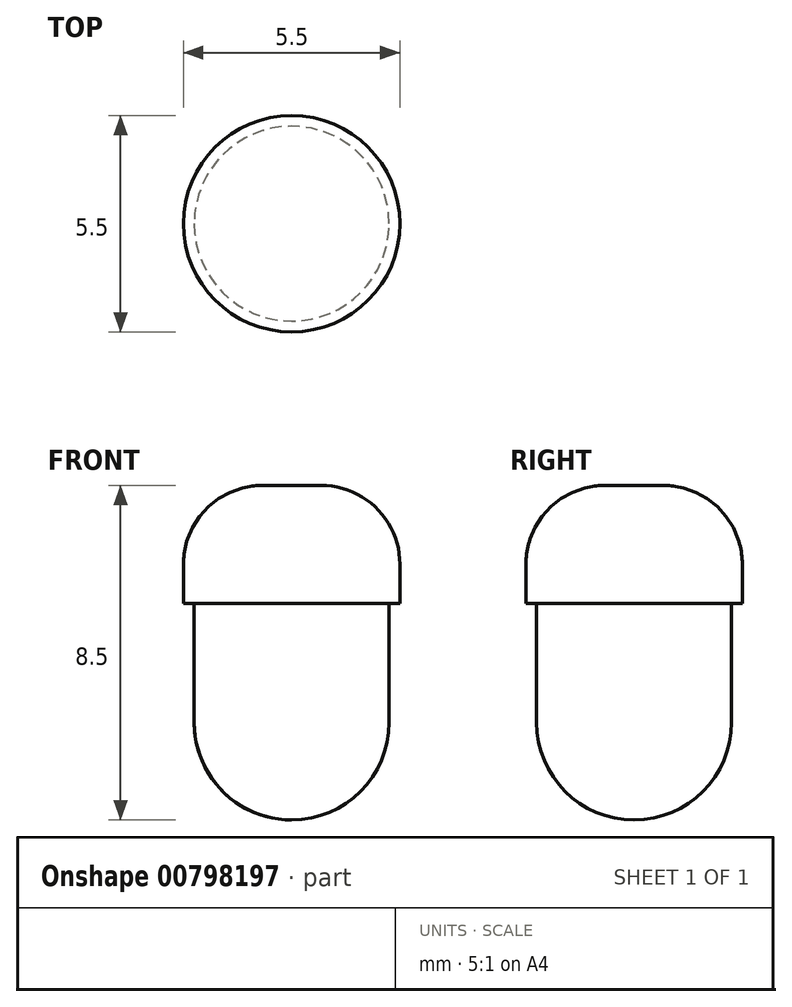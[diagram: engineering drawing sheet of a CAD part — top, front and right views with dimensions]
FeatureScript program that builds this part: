
annotation { "Feature Type Name" : "Feature", "Feature Type Description" : "" }
export const myFeature = defineFeature(function(context is Context, id is Id, definition is map)
    precondition{}
    {
        {
            var Q0;
            Q0=qCreatedBy(makeId("Top.planeOp"),FACE);
            var sketch = newSketch(context, id + "F0", { "sketchPlane" : qUnion([Q0])});
            skCircle(sketch, "E0", {"center": v(0, 0) * mm, "radius": 2.75 * mm});
            skSolve(sketch);
        }
        {
            var Q0;
            Q0 = qSketchRegion(id + "F0", true);
            extrude(context, id + "F1", {"entities" : qUnion([Q0]), "depth" : 3 * mm, "offsetDistance" : 25 * mm});
        }
        {
            var Q0;
            Q0=makeQuery(id+"F1.opExtrude","CAP_EDGE",EDGE,{"disambiguationData":[OSD([sQuery(id+"F0.wireOp",EDGE,"E0")])],"isStart":false});
            fillet(context, id + "F2", {"entities" : qUnion([Q0]), "radius" : 2 * mm, "tangentPropagation" : true, "allowEdgeOverflow" : false});
        }
        {
            var Q0;
            Q0=makeQuery(id+"F1.opExtrude","CAP_FACE",FACE,{"disambiguationData":[OSD([sQuery(id+"F0.wireOp",EDGE,"E0")])],"isStart":true});
            var sketch = newSketch(context, id + "F3", { "sketchPlane" : qUnion([Q0])});
            skCircle(sketch, "E1", {"center": v(0, 0) * mm, "radius": 2.48 * mm});
            skSolve(sketch);
        }
        {
            var Q0;
            Q0 = qSketchRegion(id + "F3", true);
            extrude(context, id + "F4", {"entities" : qUnion([Q0]), "operationType" : NewBodyOperationType.ADD, "depth" : 5.5 * mm, "offsetDistance" : 25 * mm});
        }
        {
            var Q0;
            Q0=makeQuery(id+"F4.opExtrude","CAP_FACE",FACE,{"disambiguationData":[OSD([sQuery(id+"F3.wireOp",EDGE,"E1")])],"isStart":false});
            fillet(context, id + "F5", {"entities" : qUnion([Q0]), "radius" : 2.48 * mm, "tangentPropagation" : true, "allowEdgeOverflow" : false});
        }
    });
